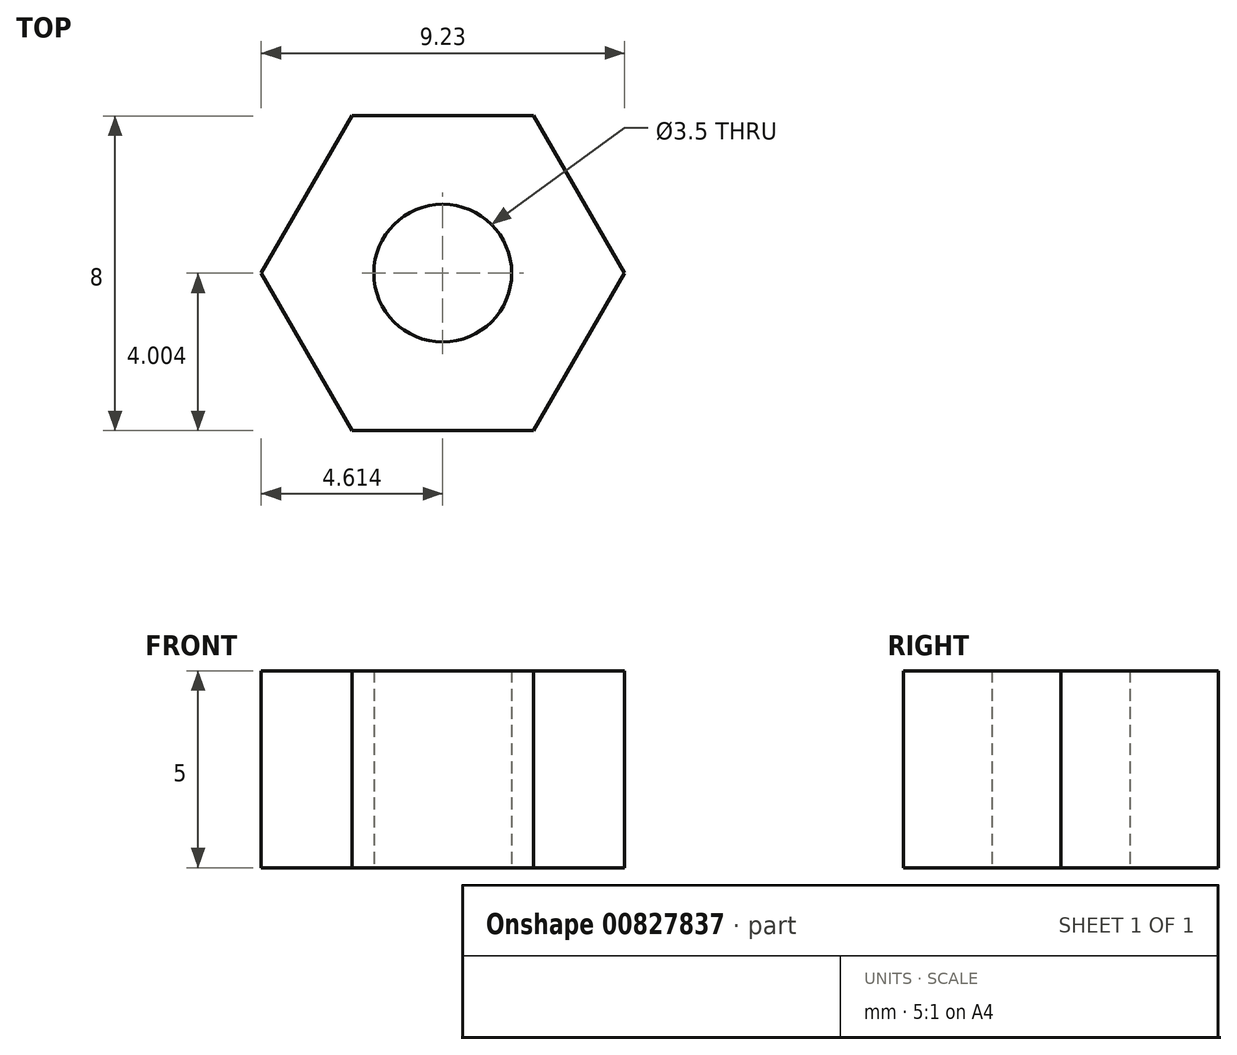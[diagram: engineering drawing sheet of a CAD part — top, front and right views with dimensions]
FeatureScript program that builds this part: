
annotation { "Feature Type Name" : "Feature", "Feature Type Description" : "" }
export const myFeature = defineFeature(function(context is Context, id is Id, definition is map)
    precondition{}
    {
        {
            var Q0;
            Q0=qCreatedBy(makeId("Top.planeOp"),FACE);
            var sketch = newSketch(context, id + "F0", { "sketchPlane" : qUnion([Q0])});
            skCircle(sketch, "E0.cCircle", {"center": v(-31, 8.75) * mm, "radius": 4 * mm, "construction": true});
            skLineSegment(sketch, "E0.0", {"start": v(-33.32, 12.75) * mm, "end": v(-28.7, 12.75) * mm});
            skLineSegment(sketch, "E0.1", {"start": v(-28.7, 12.75) * mm, "end": v(-26.39, 8.75) * mm});
            skLineSegment(sketch, "E0.2", {"start": v(-26.39, 8.75) * mm, "end": v(-28.7, 4.75) * mm});
            skLineSegment(sketch, "E0.3", {"start": v(-28.7, 4.75) * mm, "end": v(-33.32, 4.75) * mm});
            skLineSegment(sketch, "E0.4", {"start": v(-33.32, 4.75) * mm, "end": v(-35.62, 8.75) * mm});
            skLineSegment(sketch, "E0.5", {"start": v(-35.62, 8.75) * mm, "end": v(-33.32, 12.75) * mm});
            skPoint(sketch, "E0.0.midPoint", {"position": v(-31, 12.75) * mm});
            skCircle(sketch, "E1", {"center": v(-31, 8.75) * mm, "radius": 1.75 * mm});
            skSolve(sketch);
        }
        {
            var Q0;
            Q0=makeQuery(id+"F0.imprint","IMPRINT",FACE,{"disambiguationData":[TD([[makeQuery(id+"F0.imprint","IMPRINT",EDGE,{"derivedFrom":sQuery(id+"F0.wireOp",EDGE,"E0.0")}),-1.0]])]});
            extrude(context, id + "F1", {"entities" : qUnion([Q0]), "depth" : 5 * mm, "offsetDistance" : 25.4 * mm});
        }
    });
